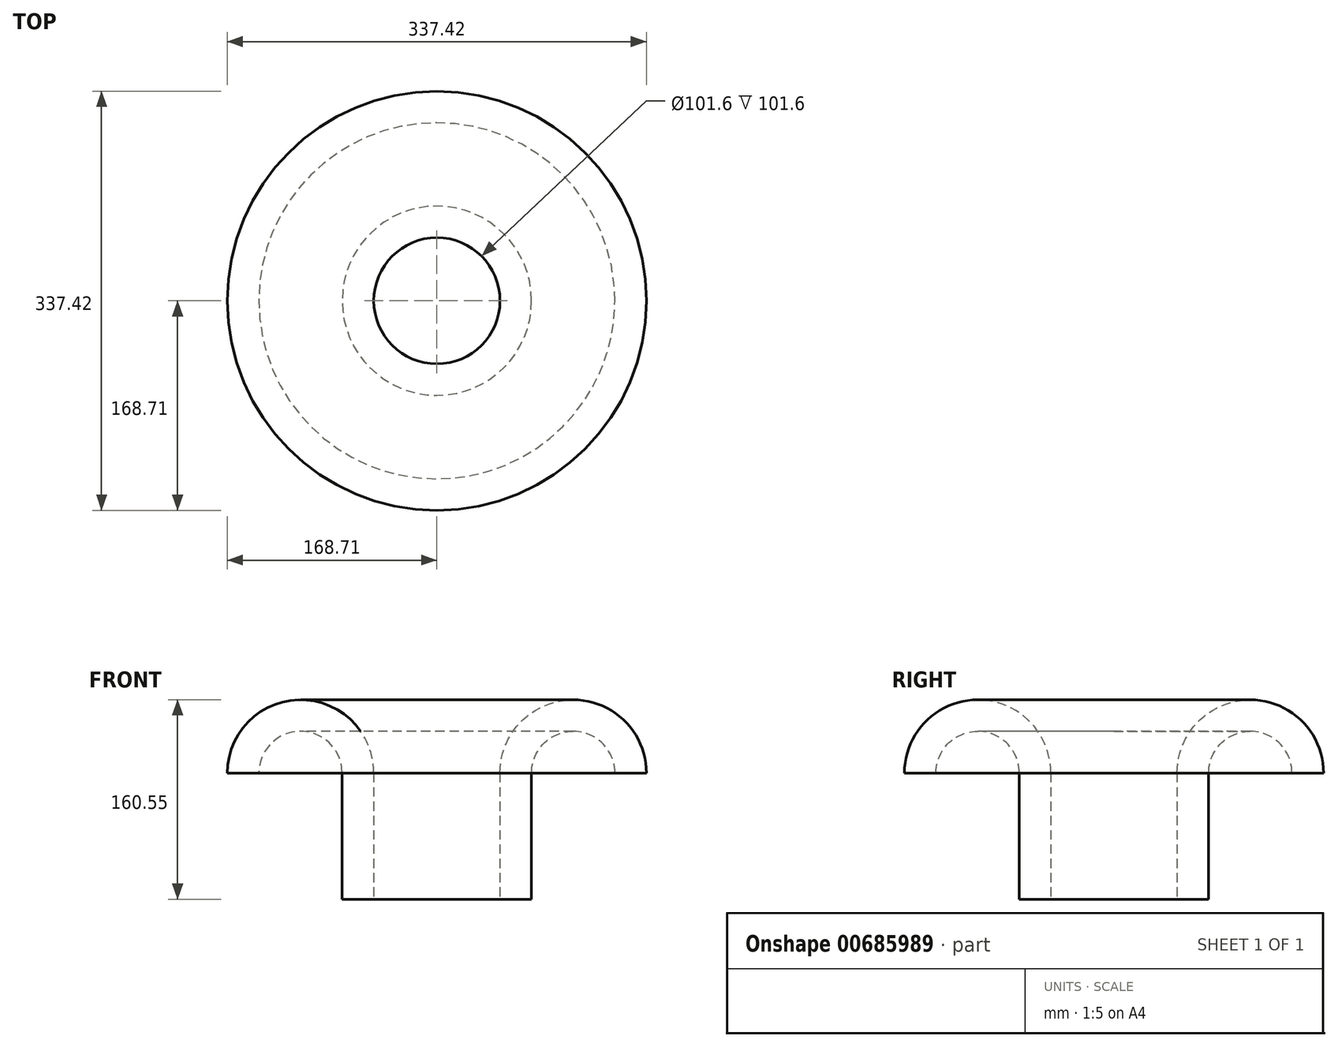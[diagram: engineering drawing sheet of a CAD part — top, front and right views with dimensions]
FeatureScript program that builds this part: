
annotation { "Feature Type Name" : "Feature", "Feature Type Description" : "" }
export const myFeature = defineFeature(function(context is Context, id is Id, definition is map)
    precondition{}
    {
        {
            var Q0;
            Q0=qCreatedBy(makeId("Front.planeOp"),FACE);
            var sketch = newSketch(context, id + "F0", { "sketchPlane" : qUnion([Q0])});
            skLineSegment(sketch, "E0", {"start": v(0, 0) * mm, "end": v(0, 101.6) * mm});
            skArc(sketch, "E1", {"start": v(0, 101.6) * mm, "mid": v(-33.55, 135.15) * mm, "end": v(-67.1, 101.6) * mm});
            skArc(sketch, "E2.0", {"start": v(25.4, 101.6) * mm, "mid": v(-33.55, 160.55) * mm, "end": v(-92.5, 101.6) * mm});
            skLineSegment(sketch, "E2.1", {"start": v(25.4, 0) * mm, "end": v(25.4, 101.6) * mm});
            skLineSegment(sketch, "E3", {"start": v(-67.1, 101.6) * mm, "end": v(-92.5, 101.6) * mm});
            skLineSegment(sketch, "E4", {"start": v(25.4, 0) * mm, "end": v(0, 0) * mm});
            skLineSegment(sketch, "E5", {"start": v(76.2, 0) * mm, "end": v(76.2, 73.95) * mm});
            skSolve(sketch);
        }
        {
            var Q0;
            Q0=makeQuery(id+"F0.imprint","IMPRINT",FACE,{"disambiguationData":[TD([[makeQuery(id+"F0.imprint","IMPRINT",EDGE,{"derivedFrom":sQuery(id+"F0.wireOp",EDGE,"E0")}),-1.0]])]});
            var Q1;
            Q1=sQuery(id+"F0.wireOp",EDGE,"E5");
            revolve(context, id + "F1", {"entities" : qUnion([Q0]), "axis" : qUnion([Q1]), "revolveType" : RevolveType.FULL});
        }
    });
